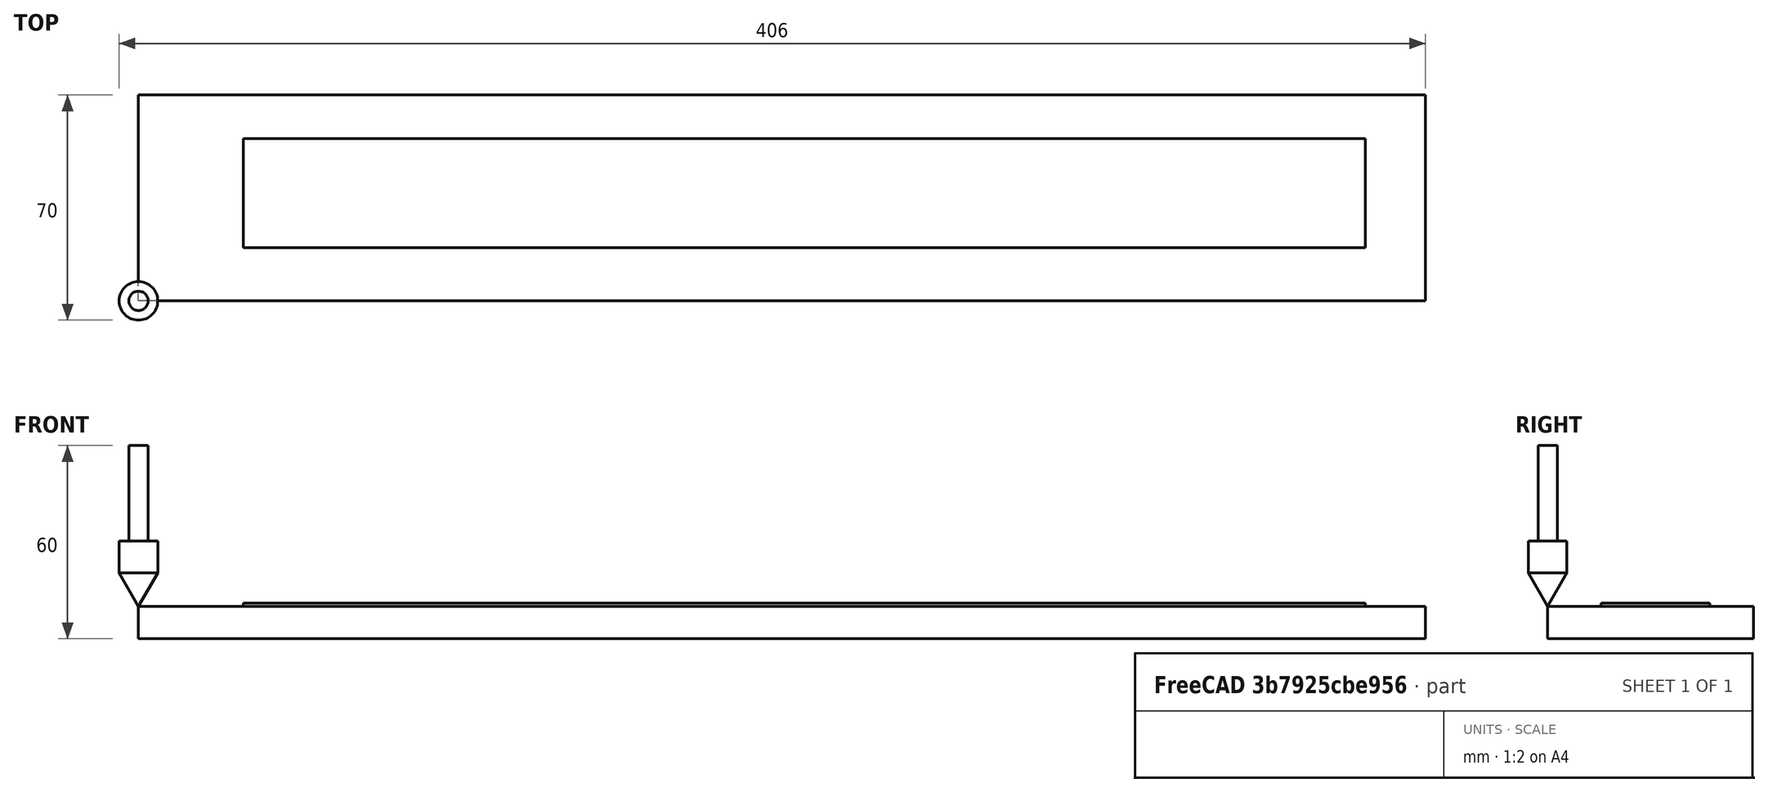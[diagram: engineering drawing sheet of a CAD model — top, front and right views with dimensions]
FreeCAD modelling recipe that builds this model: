
FCSTD DOCUMENT  (FreeCAD 0.21R33694 (Git))
Label: BoyneTannum
License: All rights reserved
LicenseURL: http://en.wikipedia.org/wiki/All_rights_reserved
objects: App::DocumentObjectGroup×3, Path::FeaturePython×3, Part::Part2DObjectPython×2, Part::FeaturePython×2, Sketcher::SketchObject×1, PartDesign::Pad×1, PartDesign::Body×1, App::FeaturePython×1, App::MeasureDistance×1, Mesh::FeaturePython×1
note: 8 computed .brp shape members not serialized (recipe doc carries the construction recipe); baked Part::Feature solids carry a one-line shape summary decoded from their .brp

FEATURE [Sketcher::SketchObject] Sketch
  FullyConstrained = true
  MapMode = 5
  Support = -> [XY_Plane]
  sketch-geometry (4):
    g0: LineSegment StartX=0 StartY=64 StartZ=0 EndX=400 EndY=64 EndZ=0
    g1: LineSegment StartX=400 StartY=64 StartZ=0 EndX=400 EndY=0 EndZ=0
    g2: LineSegment StartX=400 StartY=0 StartZ=0 EndX=0 EndY=0 EndZ=0
    g3: LineSegment StartX=0 StartY=0 StartZ=0 EndX=0 EndY=64 EndZ=0
  constraints (12):
    c: Coincident(g0,g1)
    c: Coincident(g1,g2)
    c: Coincident(g2,g3)
    c: Coincident(g3,g0)
    c: Horizontal(g0)
    c: Horizontal(g2)
    c: Vertical(g1)
    c: Vertical(g3)
    c: PointOnObject(g0,g-2)
    c: PointOnObject(g2,g-1)
    c: DistanceX(g2,g2) = 400
    c: DistanceY(g3,g3) = 64
FEATURE [PartDesign::Pad] Pad
  Direction = (0,0,1)
  Length = 10
  Length2 = 10
  Profile = -> Sketch
  ReferenceAxis = -> Sketch [N_Axis]
  Reversed = true
  Type = 0
FEATURE [PartDesign::Body] Body
  Group = -> [Sketch,Pad]
  Origin = -> Origin
  Tip = -> Pad
FEATURE [Part::Part2DObjectPython] ShapeString  # Draft 2D object (typed FeaturePython)
  FontFile = <path>
  MakeFace = true
  Placement = pos=(28.95,16.94,0) rot=(0,0,1;0rad)
  Size = 42
  String = BOYNE TANNUM
  Tracking = 0
FEATURE [App::FeaturePython] SetupSheet  # Path/CAM operation (typed FeaturePython)
  ClearanceHeightExpression = OpStockZMax+SetupSheet.ClearanceHeightOffset
  ClearanceHeightOffset = 5
  CoolantMode = 0
  CoolantModes = None | Flood | Mist
  FinalDepthExpression = OpFinalDepth
  HorizRapid = 0
  SafeHeightExpression = OpStockZMax+SetupSheet.SafeHeightOffset
  SafeHeightOffset = 3
  StartDepthExpression = OpStartDepth
  StepDownExpression = OpToolDiameter
  VertRapid = 0
FEATURE [Part::Part2DObjectPython] Clone2D  label="Model-ShapeString"  # Draft 2D object (typed FeaturePython)
  Fuse = false
  Objects = -> [ShapeString]
  PathResource = Model
  Placement = pos=(28.95,16.94,0) rot=(0,0,1;0rad)
  Scale = (1,1,1)
FEATURE [App::DocumentObjectGroup] Model
  Group = -> [Clone2D]
FEATURE [Part::FeaturePython] Stock001  # WARN: FeaturePython — macro-defined, semantics opaque (R4)
  Height = 1
  Length = 348.74
  Placement = pos=(32.5788,16.562,0) rot=(0,0,1;0rad)
  StockType = CreateBox
  Width = 33.87
FEATURE [Part::FeaturePython] ToolBit001  label="60 Deg. V-Bit"  # Path/CAM toolbit (typed FeaturePython)
  BitPropertyNames = Chipload | CuttingEdgeAngle | CuttingEdgeHeight | Diameter | Flutes | Length | Material | ShankDiameter | TipDiameter
  BitShape = /app/freecad/Mod/Path/Tools/Shape/v-bit.fcstd
  Chipload = 0
  CuttingEdgeAngle = 60
  CuttingEdgeHeight = 10
  Diameter = 12
  File = <userpath>/Documents/Sherline/FreeCAD/Bit/60degree_Vbit.fctb
  Flutes = 2
  Length = 50
  Material = 0
  ShankDiameter = 6
  ShapeName = v_bit
  TipDiameter = 0.01
FEATURE [Path::FeaturePython] _0_Deg__V_Bit  label="60 Deg. V-Bit001"  # Path/CAM operation (typed FeaturePython)
  HorizFeed = 15
  HorizRapid = 0
  SpindleDir = 0
  SpindleSpeed = 10000
  Tool = -> ToolBit001
  ToolNumber = 2
  VertFeed = 3.33333
  VertRapid = 0
  expr: HorizRapid = SetupSheet.HorizRapid
  expr: VertRapid = SetupSheet.VertRapid
FEATURE [App::DocumentObjectGroup] Tools
  Group = -> [_0_Deg__V_Bit]
FEATURE [Path::FeaturePython] Vcarve  # Path/CAM operation (typed FeaturePython)
  Active = true
  BaseShapes = -> [Clone2D]
  ClearanceHeight = 6
  Colinear = 10
  CoolantMode = 0
  CycleTime = 00:10:00
  Discretize = 0.01
  FinalDepth = -10
  OpFinalDepth = 0
  OpStartDepth = 0
  OpStockZMax = 1
  OpStockZMin = 0
  OpToolDiameter = 12
  SafeHeight = 4
  StartDepth = 0
  Tolerance = 0.01
  ToolController = -> _0_Deg__V_Bit
  expr: ClearanceHeight = OpStockZMax + SetupSheet.ClearanceHeightOffset
  expr: FinalDepth = -10
  expr: SafeHeight = OpStockZMax + SetupSheet.SafeHeightOffset
  expr: StartDepth = 0
FEATURE [App::DocumentObjectGroup] Operations
  Group = -> [Vcarve]
FEATURE [Path::FeaturePython] Job  # Path/CAM operation (typed FeaturePython)
  CycleTime = 00:10:00
  Fixtures = G54
  GeometryTolerance = 0.01
  JobType = 0
  Model = -> Model
  Operations = -> Operations
  OrderOutputBy = 0
  PostProcessor = 4
  PostProcessorOutputFile = %D/%d-%j.ngc
  SetupSheet = -> SetupSheet
  SplitOutput = false
  Stock = -> Stock001
  Tools = -> Tools
FEATURE [App::MeasureDistance] Distance  label="Distance: 3.93 mm"
  Distance = 3.92597
  P1 = (73.2657,16.6598,0)
  P2 = (73.4787,18.5803,-3.41754)
FEATURE [Mesh::FeaturePython] CutMaterial  # WARN: FeaturePython — macro-defined, semantics opaque (R4)
note: 1 file-system path scrubbed to <path> (originals preserved in the JSON sidecar)
